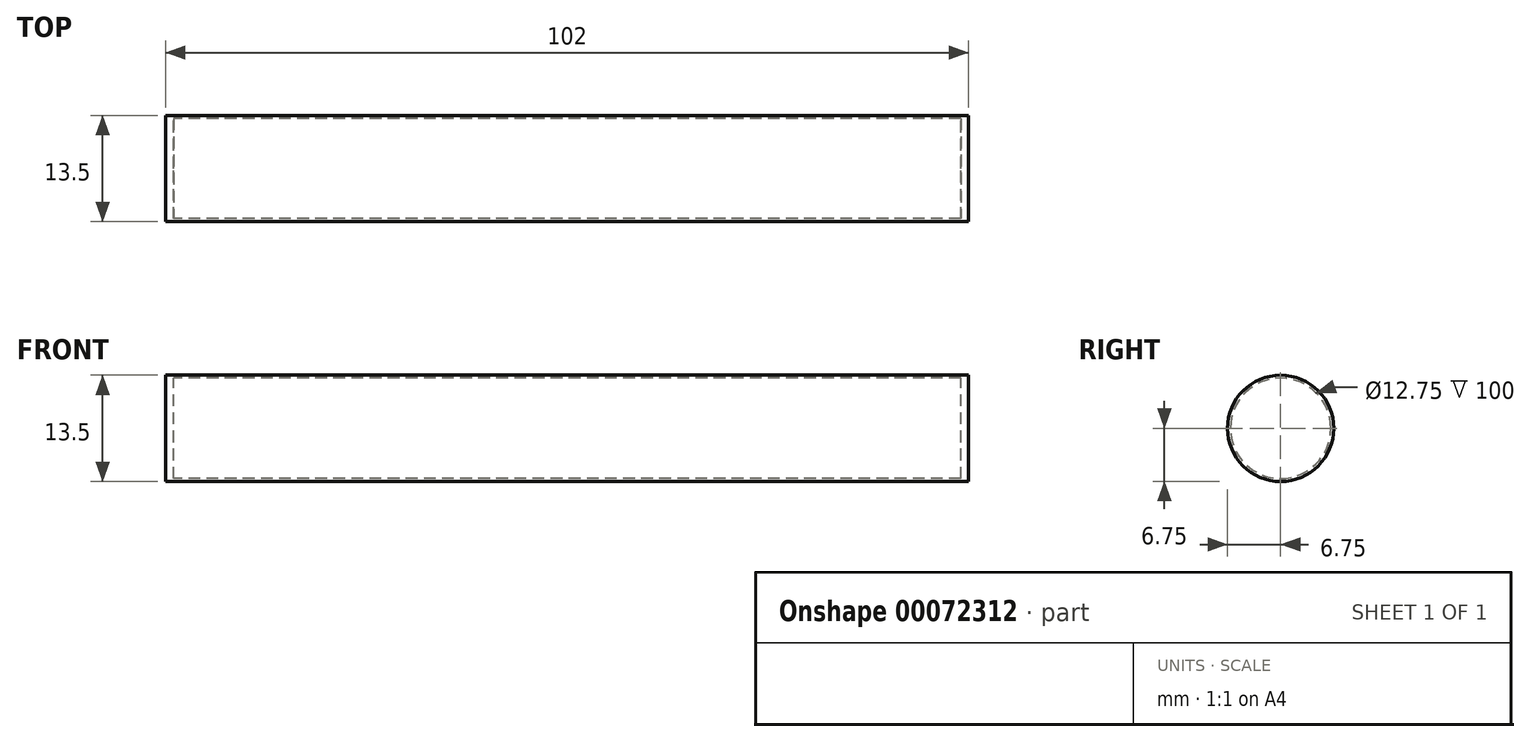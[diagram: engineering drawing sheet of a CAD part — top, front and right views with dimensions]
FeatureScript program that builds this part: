
annotation { "Feature Type Name" : "Feature", "Feature Type Description" : "" }
export const myFeature = defineFeature(function(context is Context, id is Id, definition is map)
    precondition{}
    {
        {
            var Q0;
            Q0=qCreatedBy(makeId("Right.planeOp"),FACE);
            var sketch = newSketch(context, id + "F0", { "sketchPlane" : qUnion([Q0])});
            skCircle(sketch, "E0", {"center": v(0, 0) * mm, "radius": 6.38 * mm});
            skCircle(sketch, "E1", {"center": v(0, 0) * mm, "radius": 6.75 * mm});
            skSolve(sketch);
        }
        {
            var Q0;
            Q0 = qSketchRegion(id + "F0", true);
            extrude(context, id + "F1", {"entities" : qUnion([Q0]), "depth" : 100 * mm});
        }
        {
            var Q0;
            Q0=makeQuery(id+"F1.opExtrude","CAP_FACE",FACE,{"disambiguationData":[OSD([sQuery(id+"F0.wireOp",EDGE,"E0"),sQuery(id+"F0.wireOp",EDGE,"E1")])],"isStart":false});
            var sketch = newSketch(context, id + "F2", { "sketchPlane" : qUnion([Q0])});
            skCircle(sketch, "E2", {"center": v(0, 0) * mm, "radius": 6.75 * mm});
            skSolve(sketch);
        }
        {
            var Q0;
            Q0 = qSketchRegion(id + "F2", true);
            extrude(context, id + "F3", {"entities" : qUnion([Q0]), "operationType" : NewBodyOperationType.ADD, "depth" : 1 * mm});
        }
        {
            var Q0;
            Q0=makeQuery(id+"F1.opExtrude","CAP_FACE",FACE,{"disambiguationData":[OSD([sQuery(id+"F0.wireOp",EDGE,"E0"),sQuery(id+"F0.wireOp",EDGE,"E1")])],"isStart":true});
            var sketch = newSketch(context, id + "F4", { "sketchPlane" : qUnion([Q0])});
            skCircle(sketch, "E3", {"center": v(0, 0) * mm, "radius": 6.75 * mm});
            skSolve(sketch);
        }
        {
            var Q0;
            Q0 = qSketchRegion(id + "F4", true);
            extrude(context, id + "F5", {"entities" : qUnion([Q0]), "operationType" : NewBodyOperationType.ADD, "depth" : 1 * mm});
        }
    });
